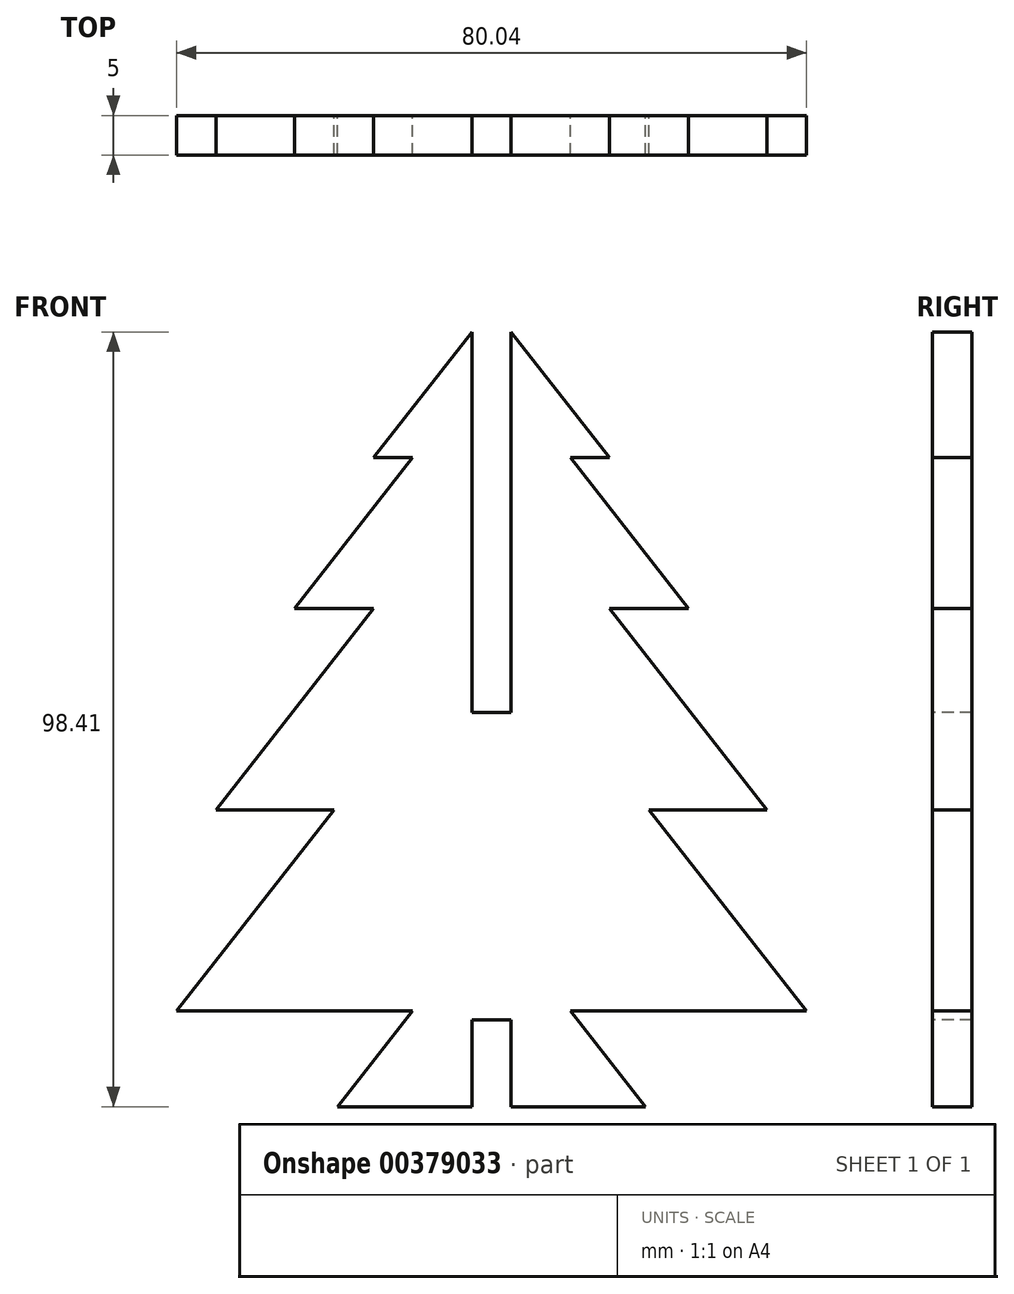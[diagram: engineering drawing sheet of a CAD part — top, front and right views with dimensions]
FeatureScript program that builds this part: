
annotation { "Feature Type Name" : "Feature", "Feature Type Description" : "" }
export const myFeature = defineFeature(function(context is Context, id is Id, definition is map)
    precondition{}
    {
        {
            var Q0;
            Q0=qCreatedBy(makeId("Front.planeOp"),FACE);
            var sketch = newSketch(context, id + "F0", { "sketchPlane" : qUnion([Q0])});
            skLineSegment(sketch, "E0", {"start": v(-23.23, -18.35) * mm, "end": v(-13.22, -18.35) * mm});
            skLineSegment(sketch, "E1", {"start": v(-13.22, -18.35) * mm, "end": v(-33.23, -18.35) * mm});
            skLineSegment(sketch, "E2", {"start": v(-33.23, -18.35) * mm, "end": v(-33.23, -6.18) * mm});
            skLineSegment(sketch, "E3", {"start": v(-13.22, -6.18) * mm, "end": v(-33.23, -6.18) * mm});
            skLineSegment(sketch, "E4", {"start": v(-13.22, -6.18) * mm, "end": v(-13.22, -18.35) * mm});
            skLineSegment(sketch, "E5", {"start": v(-23.23, -18.35) * mm, "end": v(-23.23, -6.18) * mm});
            skLineSegment(sketch, "E6", {"start": v(-33.23, -6.18) * mm, "end": v(-63.25, -6.18) * mm});
            skLineSegment(sketch, "E7", {"start": v(-13.22, -6.18) * mm, "end": v(16.8, -6.18) * mm});
            skLineSegment(sketch, "E8", {"start": v(-63.25, -6.18) * mm, "end": v(-43.24, 19.37) * mm});
            skLineSegment(sketch, "E9", {"start": v(-43.24, 19.37) * mm, "end": v(-3.22, 19.37) * mm});
            skLineSegment(sketch, "E10", {"start": v(-3.22, 19.37) * mm, "end": v(16.8, -6.18) * mm});
            skLineSegment(sketch, "E11", {"start": v(-23.23, -6.18) * mm, "end": v(-23.23, 19.37) * mm});
            skLineSegment(sketch, "E12", {"start": v(-43.24, 19.37) * mm, "end": v(-58.24, 19.37) * mm});
            skLineSegment(sketch, "E13", {"start": v(-58.24, 19.37) * mm, "end": v(-38.23, 44.92) * mm});
            skLineSegment(sketch, "E14", {"start": v(-3.22, 19.37) * mm, "end": v(11.8, 19.37) * mm});
            skLineSegment(sketch, "E15", {"start": v(11.8, 19.37) * mm, "end": v(-8.22, 44.92) * mm});
            skLineSegment(sketch, "E16", {"start": v(-8.22, 44.92) * mm, "end": v(-38.23, 44.92) * mm});
            skLineSegment(sketch, "E17", {"start": v(-23.23, 19.37) * mm, "end": v(-23.23, 44.92) * mm});
            skLineSegment(sketch, "E18", {"start": v(-38.23, 44.92) * mm, "end": v(-48.24, 44.92) * mm});
            skLineSegment(sketch, "E19", {"start": v(-48.24, 44.92) * mm, "end": v(-33.23, 64.09) * mm});
            skLineSegment(sketch, "E20", {"start": v(-33.23, 64.09) * mm, "end": v(-13.22, 64.09) * mm});
            skLineSegment(sketch, "E21", {"start": v(-13.22, 64.09) * mm, "end": v(1.79, 44.92) * mm});
            skLineSegment(sketch, "E22", {"start": v(1.79, 44.92) * mm, "end": v(-8.22, 44.92) * mm});
            skLineSegment(sketch, "E23", {"start": v(-33.23, 64.09) * mm, "end": v(-38.23, 64.09) * mm});
            skLineSegment(sketch, "E24", {"start": v(-38.23, 64.09) * mm, "end": v(-23.23, 83.25) * mm});
            skLineSegment(sketch, "E25", {"start": v(-23.23, 83.25) * mm, "end": v(-8.22, 64.09) * mm});
            skLineSegment(sketch, "E26", {"start": v(-8.22, 64.09) * mm, "end": v(-13.22, 64.09) * mm});
            skLineSegment(sketch, "E27", {"start": v(-63.25, -6.18) * mm, "end": v(-23.23, -6.18) * mm});
            skLineSegment(sketch, "E28", {"start": v(-23.23, -6.18) * mm, "end": v(16.8, -6.18) * mm});
            skLineSegment(sketch, "E29", {"start": v(-33.23, -18.35) * mm, "end": v(-42.76, -18.35) * mm});
            skLineSegment(sketch, "E30", {"start": v(-42.76, -18.35) * mm, "end": v(-33.23, -6.18) * mm});
            skLineSegment(sketch, "E31", {"start": v(-13.22, -18.35) * mm, "end": v(-3.7, -18.35) * mm});
            skLineSegment(sketch, "E32", {"start": v(-3.7, -18.35) * mm, "end": v(-13.22, -6.18) * mm});
            skLineSegment(sketch, "E33", {"start": v(-33.23, -6.18) * mm, "end": v(-48.24, -6.18) * mm});
            skLineSegment(sketch, "E34", {"start": v(-13.22, -6.18) * mm, "end": v(1.79, -6.18) * mm});
            skLineSegment(sketch, "E35", {"start": v(-23.23, 19.37) * mm, "end": v(-3.22, 19.37) * mm});
            skSolve(sketch);
        }
        {
            var Q0;
            Q0=makeQuery(id+"F0.imprint","IMPRINT",FACE,{"disambiguationData":[TD([[makeQuery(id+"F0.imprint","IMPRINT",EDGE,{"derivedFrom":sQuery(id+"F0.wireOp",EDGE,"E20")}),1.0]])]});
            var Q1;
            {var subQ0=sQuery(id+"F0.wireOp",EDGE,"E18");Q1=makeQuery(id+"F0.imprint","IMPRINT",FACE,{"disambiguationData":[TD([[makeQuery(id+"F0.imprint","IMPRINT",EDGE,{"derivedFrom":subQ0}),-1.0]])]});}
            var Q2;
            {var subQ3=sQuery(id+"F0.wireOp",EDGE,"E12");Q2=makeQuery(id+"F0.imprint","IMPRINT",FACE,{"disambiguationData":[TD([[makeQuery(id+"F0.imprint","IMPRINT",EDGE,{"derivedFrom":subQ3}),-1.0]])]});}
            var Q3;
            {var subQ3=sQuery(id+"F0.wireOp",EDGE,"E14");Q3=makeQuery(id+"F0.imprint","IMPRINT",FACE,{"disambiguationData":[TD([[makeQuery(id+"F0.imprint","IMPRINT",EDGE,{"derivedFrom":subQ3}),1.0]])]});}
            var Q4;
            {var subQ3=sQuery(id+"F0.wireOp",EDGE,"E8");Q4=makeQuery(id+"F0.imprint","IMPRINT",FACE,{"disambiguationData":[TD([[makeQuery(id+"F0.imprint","IMPRINT",EDGE,{"derivedFrom":subQ3}),-1.0]])]});}
            var Q5;
            {var subQ3=sQuery(id+"F0.wireOp",EDGE,"E10");Q5=makeQuery(id+"F0.imprint","IMPRINT",FACE,{"disambiguationData":[TD([[makeQuery(id+"F0.imprint","IMPRINT",EDGE,{"derivedFrom":subQ3}),-1.0]])]});}
            var Q6;
            Q6=makeQuery(id+"F0.imprint","IMPRINT",FACE,{"disambiguationData":[TD([[makeQuery(id+"F0.imprint","IMPRINT",EDGE,{"derivedFrom":sQuery(id+"F0.wireOp",EDGE,"E2")}),1.0]])]});
            var Q7;
            {var subQ0=sQuery(id+"F0.wireOp",EDGE,"E2");Q7=makeQuery(id+"F0.imprint","IMPRINT",FACE,{"disambiguationData":[TD([[makeQuery(id+"F0.imprint","IMPRINT",EDGE,{"derivedFrom":subQ0}),-1.0]])]});}
            var Q8;
            {var subQ0=sQuery(id+"F0.wireOp",EDGE,"E4");Q8=makeQuery(id+"F0.imprint","IMPRINT",FACE,{"disambiguationData":[TD([[makeQuery(id+"F0.imprint","IMPRINT",EDGE,{"derivedFrom":subQ0}),-1.0]])]});}
            var Q9;
            Q9=makeQuery(id+"F0.imprint","IMPRINT",FACE,{"disambiguationData":[TD([[makeQuery(id+"F0.imprint","IMPRINT",EDGE,{"derivedFrom":sQuery(id+"F0.wireOp",EDGE,"E4")}),1.0]])]});
            extrude(context, id + "F1", {"entities" : qUnion([Q0, Q1, Q2, Q3, Q4, Q5, Q6, Q7, Q8, Q9]), "flatOperationType" : FlatOperationType.REMOVE, "offsetDistance" : 25 * mm, "depth" : 5 * mm, "domain" : OperationDomain.MODEL});
        }
        {
            var Q0;
            Q0=makeQuery(id+"F1.opExtrude","CAP_FACE",FACE,{"disambiguationData":[OSD([sQuery(id+"F0.wireOp",EDGE,"E1"),sQuery(id+"F0.wireOp",EDGE,"E8"),sQuery(id+"F0.wireOp",EDGE,"E10"),sQuery(id+"F0.wireOp",EDGE,"E12"),sQuery(id+"F0.wireOp",EDGE,"E13"),sQuery(id+"F0.wireOp",EDGE,"E14"),sQuery(id+"F0.wireOp",EDGE,"E15"),sQuery(id+"F0.wireOp",EDGE,"E18"),sQuery(id+"F0.wireOp",EDGE,"E19"),sQuery(id+"F0.wireOp",EDGE,"E21"),sQuery(id+"F0.wireOp",EDGE,"E22"),sQuery(id+"F0.wireOp",EDGE,"E23"),sQuery(id+"F0.wireOp",EDGE,"E24"),sQuery(id+"F0.wireOp",EDGE,"E25"),sQuery(id+"F0.wireOp",EDGE,"E26"),sQuery(id+"F0.wireOp",EDGE,"E27"),sQuery(id+"F0.wireOp",EDGE,"E28"),sQuery(id+"F0.wireOp",EDGE,"E29"),sQuery(id+"F0.wireOp",EDGE,"E30"),sQuery(id+"F0.wireOp",EDGE,"E31"),sQuery(id+"F0.wireOp",EDGE,"E32")])],"isStart":false});
            var sketch = newSketch(context, id + "F2", { "sketchPlane" : qUnion([Q0])});
            skLineSegment(sketch, "E36", {"start": v(-23.23, -18.35) * mm, "end": v(-23.23, -7.35) * mm});
            skLineSegment(sketch, "E37", {"start": v(-23.23, 83.25) * mm, "end": v(-23.23, 31.75) * mm});
            skLineSegment(sketch, "E38.bottom", {"start": v(-20.73, 83.25) * mm, "end": v(-25.73, 83.25) * mm});
            skLineSegment(sketch, "E38.top", {"start": v(-20.73, 31.75) * mm, "end": v(-25.73, 31.75) * mm});
            skLineSegment(sketch, "E38.left", {"start": v(-20.73, 83.25) * mm, "end": v(-20.73, 31.75) * mm});
            skLineSegment(sketch, "E38.right", {"start": v(-25.73, 83.25) * mm, "end": v(-25.73, 31.75) * mm});
            skPoint(sketch, "E38.middle", {"position": v(-23.23, 57.5) * mm});
            skLineSegment(sketch, "E39.bottom", {"start": v(-20.73, -18.35) * mm, "end": v(-25.73, -18.35) * mm});
            skLineSegment(sketch, "E39.top", {"start": v(-20.73, -7.35) * mm, "end": v(-25.73, -7.35) * mm});
            skLineSegment(sketch, "E39.left", {"start": v(-20.73, -18.35) * mm, "end": v(-20.73, -7.35) * mm});
            skLineSegment(sketch, "E39.right", {"start": v(-25.73, -18.35) * mm, "end": v(-25.73, -7.35) * mm});
            skPoint(sketch, "E39.middle", {"position": v(-23.23, -12.85) * mm});
            skSolve(sketch);
        }
        {
            var Q0;
            {var subQ0=sQuery(id+"F2.wireOp",EDGE,"E37");Q0=makeQuery(id+"F2.imprint","IMPRINT",FACE,{"disambiguationData":[TD([[makeQuery(id+"F2.imprint","IMPRINT",EDGE,{"derivedFrom":subQ0}),-1.0]])]});}
            var Q1;
            {var subQ0=sQuery(id+"F2.wireOp",EDGE,"E36");Q1=makeQuery(id+"F2.imprint","IMPRINT",FACE,{"disambiguationData":[TD([[makeQuery(id+"F2.imprint","IMPRINT",EDGE,{"derivedFrom":subQ0}),1.0]])]});}
            var Q2;
            {var subQ0=sQuery(id+"F2.wireOp",EDGE,"E36");Q2=makeQuery(id+"F2.imprint","IMPRINT",FACE,{"disambiguationData":[TD([[makeQuery(id+"F2.imprint","IMPRINT",EDGE,{"derivedFrom":subQ0}),-1.0]])]});}
            var Q3;
            {var subQ0=sQuery(id+"F2.wireOp",EDGE,"E37");Q3=makeQuery(id+"F2.imprint","IMPRINT",FACE,{"disambiguationData":[TD([[makeQuery(id+"F2.imprint","IMPRINT",EDGE,{"derivedFrom":subQ0}),1.0]])]});}
            extrude(context, id + "F3", {"entities" : qUnion([Q0, Q1, Q2, Q3]), "operationType" : NewBodyOperationType.REMOVE, "flatOperationType" : FlatOperationType.REMOVE, "oppositeDirection" : true, "offsetDistance" : 25 * mm, "depth" : 25 * mm, "domain" : OperationDomain.MODEL});
        }
    });
